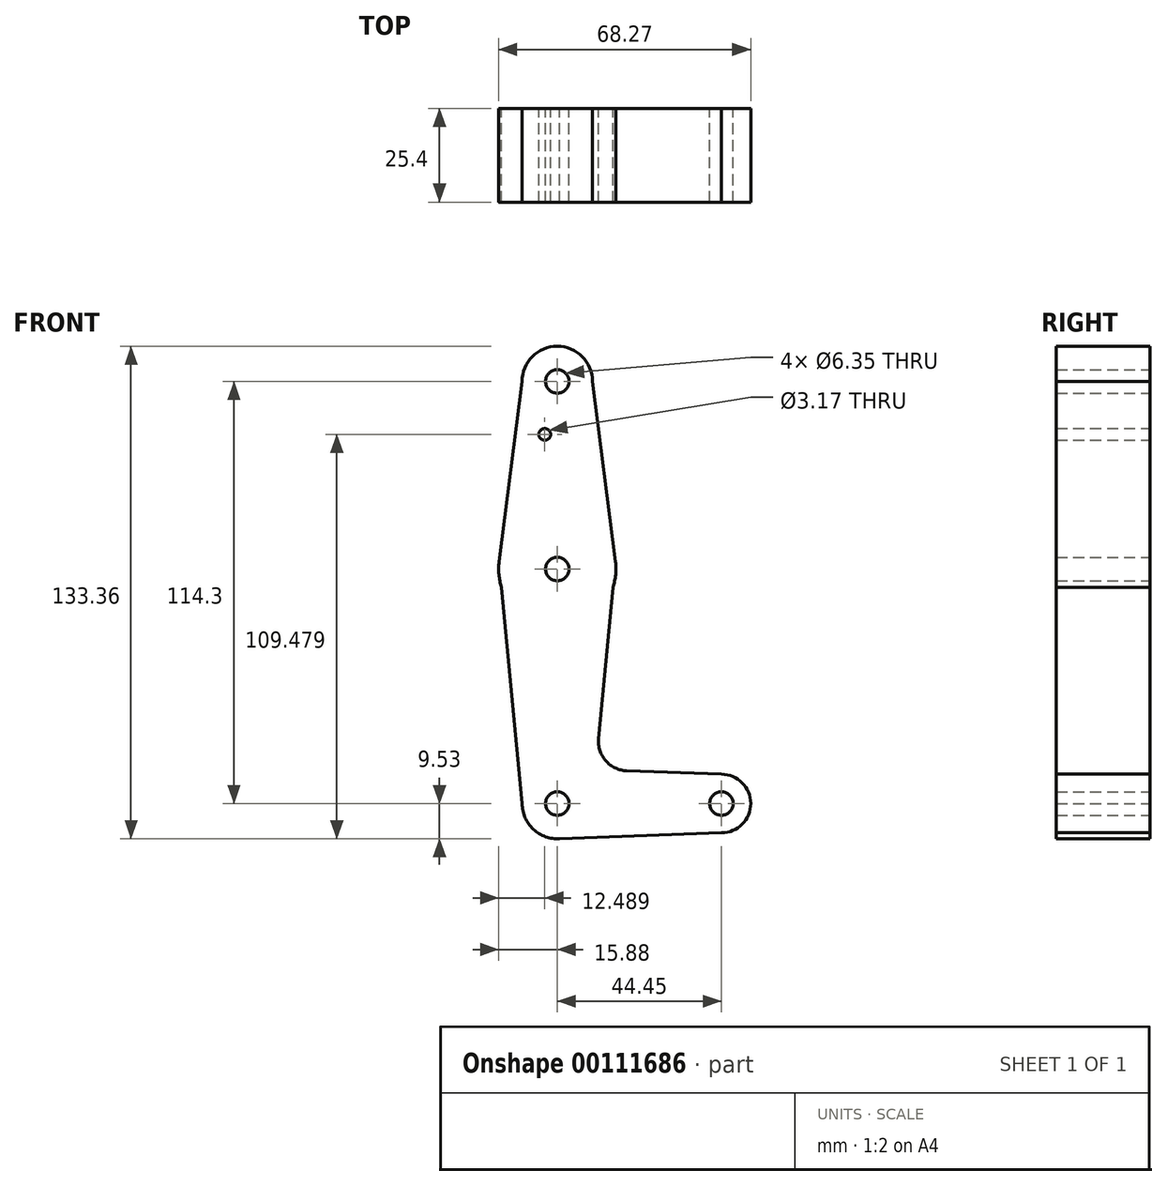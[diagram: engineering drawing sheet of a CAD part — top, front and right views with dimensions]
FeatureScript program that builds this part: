
annotation { "Feature Type Name" : "Feature", "Feature Type Description" : "" }
export const myFeature = defineFeature(function(context is Context, id is Id, definition is map)
    precondition{}
    {
        {
            var Q0;
            Q0=qCreatedBy(makeId("Front.planeOp"),FACE);
            var sketch = newSketch(context, id + "F0", { "sketchPlane" : qUnion([Q0])});
            skLineSegment(sketch, "E0", {"start": v(0, 0) * mm, "end": v(44.45, 0) * mm, "construction": true});
            skCircle(sketch, "E1", {"center": v(0, 63.5) * mm, "radius": 15.88 * mm});
            skCircle(sketch, "E2", {"center": v(0, 0) * mm, "radius": 9.53 * mm});
            skLineSegment(sketch, "E3", {"start": v(0, 0) * mm, "end": v(0, 114.3) * mm, "construction": true});
            skCircle(sketch, "E4", {"center": v(0, 114.3) * mm, "radius": 9.53 * mm});
            skCircle(sketch, "E5", {"center": v(44.45, 0) * mm, "radius": 7.94 * mm});
            skLineSegment(sketch, "E6", {"start": v(-9.52, 114.3) * mm, "end": v(-15.75, 65.5) * mm});
            skLineSegment(sketch, "E7", {"start": v(-15.75, 65.5) * mm, "end": v(-9.52, 0) * mm});
            skLineSegment(sketch, "E8", {"start": v(9.53, 114.3) * mm, "end": v(15.75, 65.5) * mm});
            skLineSegment(sketch, "E9", {"start": v(15.75, 65.5) * mm, "end": v(11.2, 17.55) * mm});
            skLineSegment(sketch, "E10", {"start": v(18.82, 8.85) * mm, "end": v(44.45, 7.94) * mm});
            skLineSegment(sketch, "E11", {"start": v(0, -9.52) * mm, "end": v(44.45, -7.94) * mm});
            skArc(sketch, "E12.filletArc", {"start": v(11.2, 17.55) * mm, "mid": v(13.13, 11.55) * mm, "end": v(18.82, 8.85) * mm});
            skCircle(sketch, "E13", {"center": v(0, 114.3) * mm, "radius": 3.18 * mm});
            skCircle(sketch, "E14", {"center": v(0, 63.5) * mm, "radius": 3.18 * mm});
            skCircle(sketch, "E15", {"center": v(0, 0) * mm, "radius": 3.18 * mm});
            skCircle(sketch, "E16", {"center": v(44.45, 0) * mm, "radius": 3.18 * mm});
            skCircle(sketch, "E17", {"center": v(-3.4, 99.95) * mm, "radius": 1.59 * mm});
            skSolve(sketch);
        }
        {
            var Q0;
            Q0 = qSketchRegion(id + "F0", true);
            extrude(context, id + "F1", {"entities" : qUnion([Q0]), "depth" : 25.4 * mm});
        }
    });
